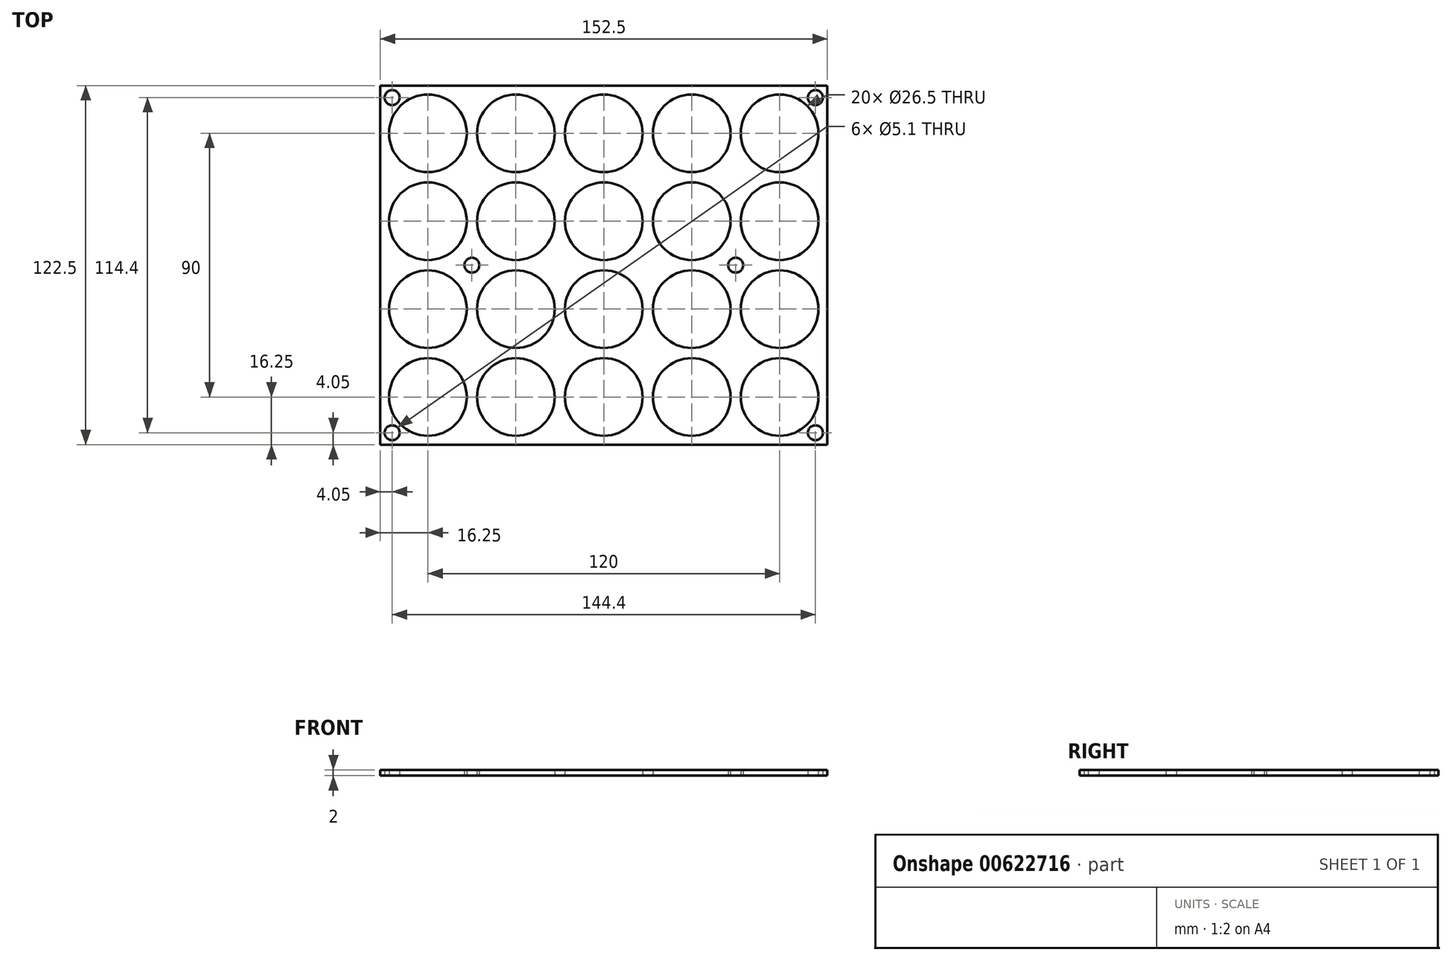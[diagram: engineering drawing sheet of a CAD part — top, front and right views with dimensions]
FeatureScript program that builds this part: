
annotation { "Feature Type Name" : "Feature", "Feature Type Description" : "" }
export const myFeature = defineFeature(function(context is Context, id is Id, definition is map)
    precondition{}
    {
        {
            var Q0;
            Q0=qCreatedBy(makeId("Top.planeOp"),FACE);
            var sketch = newSketch(context, id + "F0", { "sketchPlane" : qUnion([Q0])});
            skLineSegment(sketch, "E0.bottom", {"start": v(-76.25, 61.25) * mm, "end": v(76.25, 61.25) * mm});
            skLineSegment(sketch, "E0.top", {"start": v(-76.25, -61.25) * mm, "end": v(76.25, -61.25) * mm});
            skLineSegment(sketch, "E0.left", {"start": v(-76.25, 61.25) * mm, "end": v(-76.25, -61.25) * mm});
            skLineSegment(sketch, "E0.right", {"start": v(76.25, 61.25) * mm, "end": v(76.25, -61.25) * mm});
            skPoint(sketch, "E0.middle", {"position": v(0, 0) * mm});
            skCircle(sketch, "E1", {"center": v(-60, 45) * mm, "radius": 13.25 * mm});
            skCircle(sketch, "E2.0.1.0", {"center": v(-60, 15) * mm, "radius": 13.25 * mm});
            skCircle(sketch, "E2.0.2.0", {"center": v(-60, -15) * mm, "radius": 13.25 * mm});
            skCircle(sketch, "E2.0.3.0", {"center": v(-60, -45) * mm, "radius": 13.25 * mm});
            skCircle(sketch, "E2.1.0.0", {"center": v(-30, 45) * mm, "radius": 13.25 * mm});
            skCircle(sketch, "E2.1.1.0", {"center": v(-30, 15) * mm, "radius": 13.25 * mm});
            skCircle(sketch, "E2.1.2.0", {"center": v(-30, -15) * mm, "radius": 13.25 * mm});
            skCircle(sketch, "E2.1.3.0", {"center": v(-30, -45) * mm, "radius": 13.25 * mm});
            skCircle(sketch, "E2.2.0.0", {"center": v(0, 45) * mm, "radius": 13.25 * mm});
            skCircle(sketch, "E2.2.1.0", {"center": v(0, 15) * mm, "radius": 13.25 * mm});
            skCircle(sketch, "E2.2.2.0", {"center": v(0, -15) * mm, "radius": 13.25 * mm});
            skCircle(sketch, "E2.2.3.0", {"center": v(0, -45) * mm, "radius": 13.25 * mm});
            skCircle(sketch, "E2.3.0.0", {"center": v(30, 45) * mm, "radius": 13.25 * mm});
            skCircle(sketch, "E2.3.1.0", {"center": v(30, 15) * mm, "radius": 13.25 * mm});
            skCircle(sketch, "E2.3.2.0", {"center": v(30, -15) * mm, "radius": 13.25 * mm});
            skCircle(sketch, "E2.3.3.0", {"center": v(30, -45) * mm, "radius": 13.25 * mm});
            skCircle(sketch, "E2.4.0.0", {"center": v(60, 45) * mm, "radius": 13.25 * mm});
            skCircle(sketch, "E2.4.1.0", {"center": v(60, 15) * mm, "radius": 13.25 * mm});
            skCircle(sketch, "E2.4.2.0", {"center": v(60, -15) * mm, "radius": 13.25 * mm});
            skCircle(sketch, "E2.4.3.0", {"center": v(60, -45) * mm, "radius": 13.25 * mm});
            skLineSegment(sketch, "E2.direction1", {"start": v(-60, 45) * mm, "end": v(-30, 45) * mm, "construction": true});
            skLineSegment(sketch, "E2.direction2", {"start": v(-60, 45) * mm, "end": v(-60, 15) * mm, "construction": true});
            skLineSegment(sketch, "E3", {"start": v(0, 88.74) * mm, "end": v(0, -97.9) * mm, "construction": true});
            skLineSegment(sketch, "E4", {"start": v(-96.24, 0) * mm, "end": v(100.37, 0) * mm, "construction": true});
            skCircle(sketch, "E5", {"center": v(-45, 0) * mm, "radius": 2.55 * mm});
            skCircle(sketch, "E6", {"center": v(-72.2, 57.2) * mm, "radius": 2.55 * mm});
            skCircle(sketch, "E7.MirrorC", {"center": v(45, 0) * mm, "radius": 2.55 * mm});
            skCircle(sketch, "E8.MirrorC", {"center": v(72.2, 57.2) * mm, "radius": 2.55 * mm});
            skCircle(sketch, "E9.MirrorC", {"center": v(-72.2, -57.2) * mm, "radius": 2.55 * mm});
            skCircle(sketch, "E10.MirrorC", {"center": v(72.2, -57.2) * mm, "radius": 2.55 * mm});
            skSolve(sketch);
        }
        {
            var Q0;
            Q0=makeQuery(id+"F0.imprint","IMPRINT",FACE,{"disambiguationData":[TD([[makeQuery(id+"F0.imprint","IMPRINT",EDGE,{"derivedFrom":sQuery(id+"F0.wireOp",EDGE,"E0.bottom")}),-1.0]])]});
            extrude(context, id + "F1", {"entities" : qUnion([Q0]), "depth" : 2 * mm, "offsetDistance" : 25 * mm});
        }
    });
